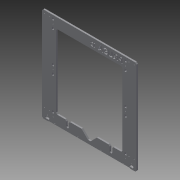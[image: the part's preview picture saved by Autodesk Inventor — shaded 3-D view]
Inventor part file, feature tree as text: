
AUTODESK INVENTOR PART (.ipt)
format: ipt  version: 2015 (Build 190159000, 159)  size: 1,157,632 bytes
history: native  units: mm
features: extrude x1, sketch x1
ambient origin geometry x8: Origin, YZ Plane, XZ Plane, XY Plane, X Axis, Y Axis, Z Axis, Center Point
bodies: Solid1 (feature_tree)
feature tree (2):
  extrude  "Extrusion1"  [1 undecoded]
  sketch  "Sketch1"  dims[d0=6.0mm d1=0.0mm]
note: 1 required parameter value undecoded (feature->parameter linkage not recoverable at this tier; creation-order binding heuristic only, values carry confidence <= 0.55)
